# Revit family: Toilet-Wall_Mount-KOHLER-REVE-K-23133T_1
name_source: partatom
category: Plumbing Fixtures
revit_build: Autodesk Revit 2017 (Build: 20160225_1515(x64)
units: mm (PartAtom-declared; Revit-internal decimal feet)

## family parameters
Cut with Voids When Loaded = No
Host = Face
OmniClass Number = 23.31.19.00
OmniClass Title = Toilets
Part Type = Normal
Room Calculation Point = No
Round Connector Dimension = Use Diameter
Shared = No

## types (2) — shared parameters
ADA Compliant = No
Apparent Load = 0 VA
Assembly Code = D2010100
CW Connection = Yes
Cold Water Inlet = Cold Water Inlet
Date Modified = 06/26/2021
Default Elevation = 0"
Electrical Connector = Yes
Electrical Note = One Dedicated Circuit Required
Finish = Kohler-Vitreous_China-0-White
Flow Rate = 0 GPM
Flush Rate- GPF = 1.18GPF
Flush Rate- LPF = 4.5LPF
HW Connection = No
Hot Water Inlet = Hot Water Inlet
Length = 21 15/16"
Manufacturer = KOHLER Co.
Master Format 2014 = 22 42 13.13
Master Format 2014 Name = Residential Water Closets
Material = Vitreous China
Pressure = 0.00 psi
Product Documentation Link = https://files.kohler.com.cn
Product Name = REVE
Product Page URL = https://www.kohler.com.cn
Seat Included = Yes
URL = https://www.kohler.com.cn
Vent Connection = No
Voltage = 220 V
Waste Connection = Yes
Waste Water Outlet = Waste Water Outlet
WaterSense Certified = No
Width = 14 3/8"

## per-type parameters (varying)
| type | Description | Model | Secondary Finish | Type |
| CPS,Flush plate-CP-Polished Chrome | Wall-hung toilet (Boming sensor AC) | K-23133T-CPS-0 | Kohler-Metal-CP-Polished_Chrome | 1 |
| BNS,Flush plate-BN-Roman Silver | Wall-hung toilet (Boming Sensor AC/Roman Silver) | K-23133T-BNS-0 | Kohler-Metal-BN-Roman_Silver | 2 |

## geometry (parser evidence)
native form markers: Sweep x8
no freeform markers — native parametric forms only
